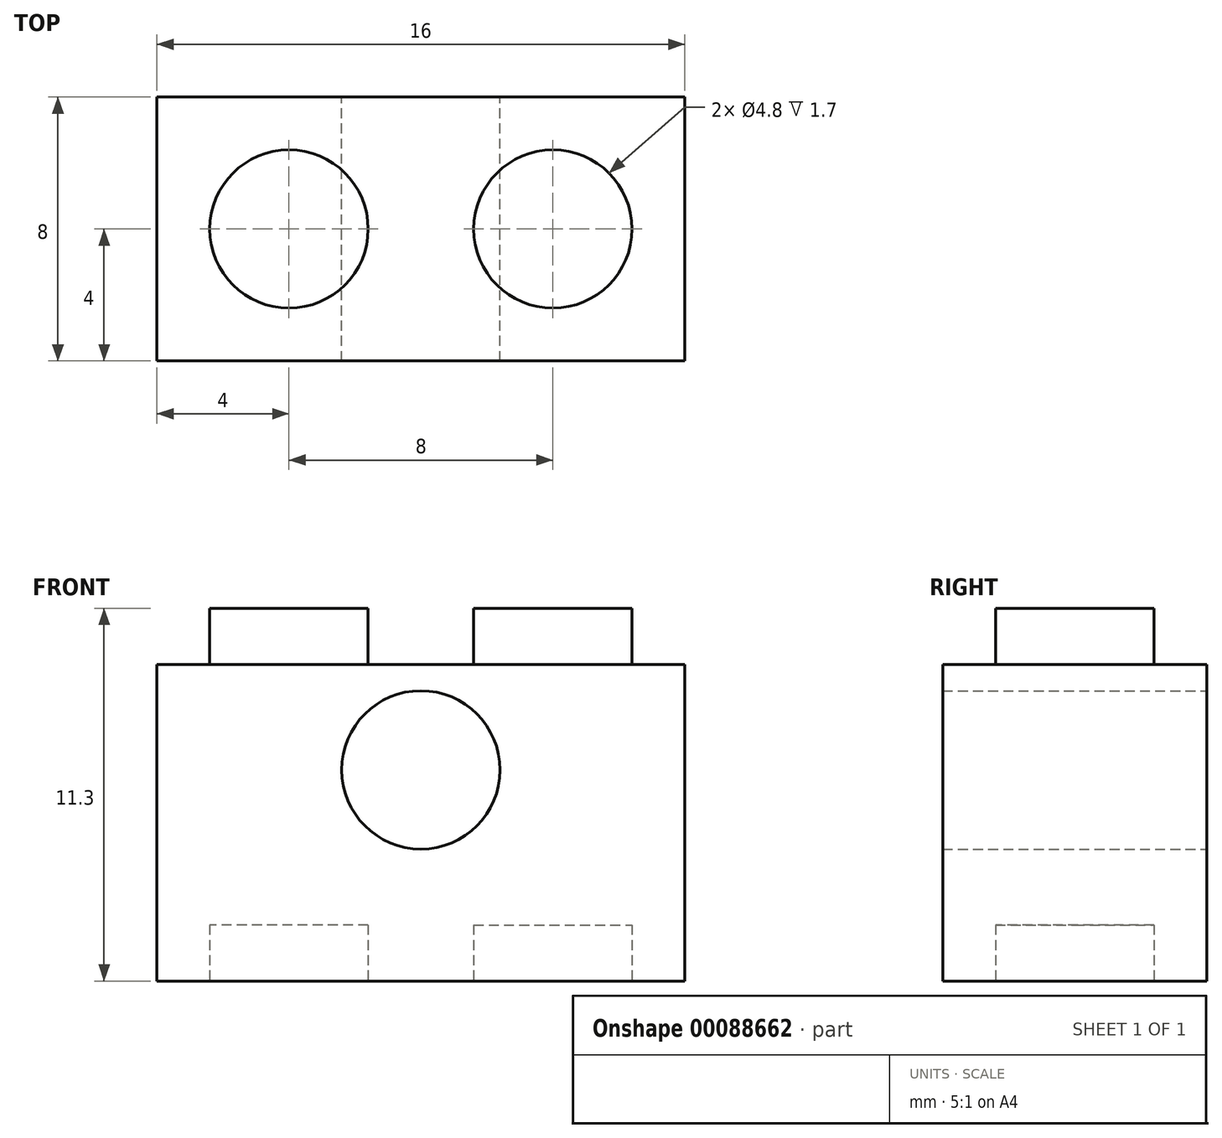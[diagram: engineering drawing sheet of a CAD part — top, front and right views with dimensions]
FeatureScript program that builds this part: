
annotation { "Feature Type Name" : "Feature", "Feature Type Description" : "" }
export const myFeature = defineFeature(function(context is Context, id is Id, definition is map)
    precondition{}
    {
        {
            var Q0;
            Q0=qCreatedBy(makeId("Front.planeOp"),FACE);
            var sketch = newSketch(context, id + "F0", { "sketchPlane" : qUnion([Q0])});
            skLineSegment(sketch, "E0.bottom", {"start": v(-4, 9.6) * mm, "end": v(-2.4, 9.6) * mm});
            skLineSegment(sketch, "E0.top", {"start": v(-4, 0) * mm, "end": v(4, 0) * mm});
            skLineSegment(sketch, "E0.left", {"start": v(-4, 9.6) * mm, "end": v(-4, 0) * mm});
            skLineSegment(sketch, "E0.right", {"start": v(4, 9.6) * mm, "end": v(4, 0) * mm});
            skLineSegment(sketch, "E1.top", {"start": v(-2.4, 11.3) * mm, "end": v(2.4, 11.3) * mm});
            skLineSegment(sketch, "E1.left", {"start": v(-2.4, 9.6) * mm, "end": v(-2.4, 11.3) * mm});
            skLineSegment(sketch, "E1.right", {"start": v(2.4, 9.6) * mm, "end": v(2.4, 11.3) * mm});
            skLineSegment(sketch, "E2", {"start": v(0, 0) * mm, "end": v(0, 24.04) * mm, "construction": true});
            skLineSegment(sketch, "E3.trimOffspring", {"start": v(2.4, 9.6) * mm, "end": v(4, 9.6) * mm});
            skSolve(sketch);
        }
        {
            var Q0;
            Q0=makeQuery(id+"F0.imprint","IMPRINT",FACE,{"disambiguationData":[TD([[makeQuery(id+"F0.imprint","IMPRINT",EDGE,{"derivedFrom":sQuery(id+"F0.wireOp",EDGE,"E0.bottom")}),-1.0]])]});
            extrude(context, id + "F1", {"entities" : qUnion([Q0]), "depth" : 8 * mm});
        }
        {
            var Q0;
            Q0=qCreatedBy(makeId("Top.planeOp"),FACE);
            var Q1;
            Q1=makeQuery(id+"F1.opExtrude","CAP_VERTEX",VERTEX,{"disambiguationData":[OSD([sQuery(id+"F0.wireOp",EDGE,"E1.top"),sQuery(id+"F0.wireOp",EDGE,"E1.right")])],"isStart":true});
            cPlane(context, id + "F2", {"entities" : qUnion([Q0, Q1]), "cplaneType" : CPlaneType.PLANE_POINT, "offset" : 152.4 * mm, "width" : 152.4 * mm, "height" : 152.4 * mm});
        }
        {
            var Q0;
            Q0=qCreatedBy(id+"F2.planeOp",FACE);
            var sketch = newSketch(context, id + "F3", { "sketchPlane" : qUnion([Q0])});
            skLineSegment(sketch, "E4.0", {"start": v(-4, -8) * mm, "end": v(-4, 0) * mm});
            skLineSegment(sketch, "E5.0", {"start": v(4, -8) * mm, "end": v(4, 0) * mm});
            skLineSegment(sketch, "E6", {"start": v(-4, 0) * mm, "end": v(4, 0) * mm});
            skLineSegment(sketch, "E7", {"start": v(-4, -8) * mm, "end": v(4, -8) * mm});
            skLineSegment(sketch, "E8", {"start": v(-4, 0) * mm, "end": v(4, -8) * mm, "construction": true});
            skLineSegment(sketch, "E9", {"start": v(-4, -8) * mm, "end": v(4, 0) * mm, "construction": true});
            skCircle(sketch, "E10", {"center": v(0, -4) * mm, "radius": 2.4 * mm});
            skSolve(sketch);
        }
        {
            var Q0;
            Q0=qSketchRegion(id+"F3",true);
            var Q1;
            Q1=makeQuery(id+"F1.opExtrude","SWEPT_FACE",FACE,{"disambiguationData":[OSD([sQuery(id+"F0.wireOp",EDGE,"E0.bottom")])]});
            extrude(context, id + "F4", {"entities" : qUnion([Q0]), "operationType" : NewBodyOperationType.REMOVE, "endBound" : BoundingType.UP_TO_SURFACE, "oppositeDirection" : true, "endBoundEntityFace" : qUnion([Q1]), "depth" : 25.4 * mm});
        }
        {
            var Q0;
            Q0=qCreatedBy(makeId("Top.planeOp"),FACE);
            var sketch = newSketch(context, id + "F5", { "sketchPlane" : qUnion([Q0])});
            skCircle(sketch, "E11.0", {"center": v(0, -4) * mm, "radius": 2.4 * mm});
            skSolve(sketch);
        }
        {
            var Q0;
            Q0=makeQuery(id+"F5.imprint","IMPRINT",FACE,{"disambiguationData":[TD([[makeQuery(id+"F5.imprint","IMPRINT",EDGE,{"derivedFrom":sQuery(id+"F5.wireOp",EDGE,"E11.0")}),1.0]])]});
            extrude(context, id + "F6", {"entities" : qUnion([Q0]), "operationType" : NewBodyOperationType.REMOVE, "depth" : 1.7 * mm});
        }
        {
            var Q0;
            Q0=qCreatedBy(makeId("Right.planeOp"),FACE);
            var Q1;
            Q1=makeQuery(id+"F1.opExtrude","CAP_VERTEX",VERTEX,{"disambiguationData":[OSD([sQuery(id+"F0.wireOp",EDGE,"E0.right"),sQuery(id+"F0.wireOp",EDGE,"E3.trimOffspring")])],"isStart":false});
            cPlane(context, id + "F7", {"entities" : qUnion([Q0, Q1]), "cplaneType" : CPlaneType.PLANE_POINT, "offset" : 152.4 * mm, "width" : 152.4 * mm, "height" : 152.4 * mm});
        }
        {
            var Q0;
            Q0=makeQuery(id+"F1.opExtrude","SWEPT_BODY",BODY,{"disambiguationData":[OSD([sQuery(id+"F0.wireOp",EDGE,"E0.bottom"),sQuery(id+"F0.wireOp",EDGE,"E0.top"),sQuery(id+"F0.wireOp",EDGE,"E0.left"),sQuery(id+"F0.wireOp",EDGE,"E0.right"),sQuery(id+"F0.wireOp",EDGE,"E1.top"),sQuery(id+"F0.wireOp",EDGE,"E1.left"),sQuery(id+"F0.wireOp",EDGE,"E1.right"),sQuery(id+"F0.wireOp",EDGE,"E3.trimOffspring")])]});
            var Q1;
            Q1=qCreatedBy(id+"F7.planeOp",FACE);
            mirror(context, id + "F8", {"operationType" : NewBodyOperationType.ADD, "entities" : qUnion([Q0]), "mirrorPlane" : qUnion([Q1])});
        }
        {
            var Q0;
            Q0=qCreatedBy(makeId("Front.planeOp"),FACE);
            var sketch = newSketch(context, id + "F9", { "sketchPlane" : qUnion([Q0])});
            skCircle(sketch, "E12", {"center": v(4, 6.4) * mm, "radius": 2.4 * mm});
            skLineSegment(sketch, "E13.0", {"start": v(-4, 9.6) * mm, "end": v(12, 9.6) * mm, "construction": true});
            skLineSegment(sketch, "E14.0", {"start": v(12, 9.6) * mm, "end": v(12, 0) * mm, "construction": true});
            skLineSegment(sketch, "E15.0", {"start": v(-4, 9.6) * mm, "end": v(-4, 0) * mm, "construction": true});
            skLineSegment(sketch, "E16.0", {"start": v(-4, 0) * mm, "end": v(12, 0) * mm, "construction": true});
            skSolve(sketch);
        }
        {
            var Q0;
            Q0 = qSketchRegion(id + "F9", true);
            extrude(context, id + "F10", {"entities" : qUnion([Q0]), "operationType" : NewBodyOperationType.REMOVE, "depth" : 25.4 * mm});
        }
    });
